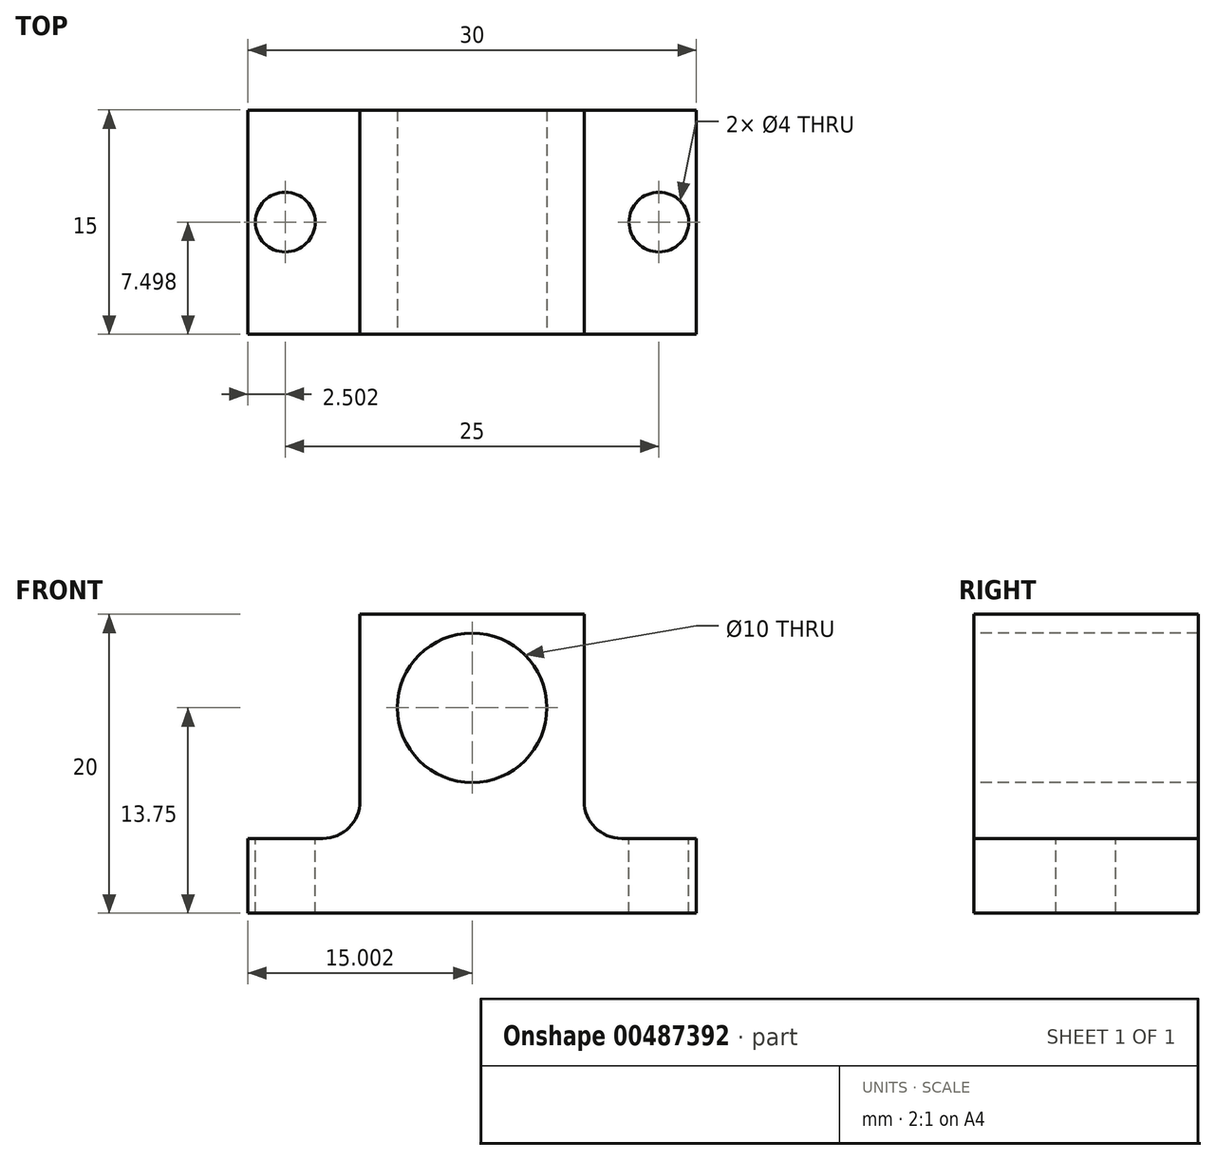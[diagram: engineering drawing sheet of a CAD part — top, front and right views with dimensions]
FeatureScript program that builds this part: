
annotation { "Feature Type Name" : "Feature", "Feature Type Description" : "" }
export const myFeature = defineFeature(function(context is Context, id is Id, definition is map)
    precondition{}
    {
        {
            var Q0;
            Q0=qCreatedBy(makeId("Top.planeOp"),FACE);
            var sketch = newSketch(context, id + "F0", { "sketchPlane" : qUnion([Q0])});
            skLineSegment(sketch, "E0.bottom", {"start": v(-19.82, 4.3) * mm, "end": v(10.18, 4.3) * mm});
            skLineSegment(sketch, "E0.top", {"start": v(-19.82, -10.7) * mm, "end": v(10.18, -10.7) * mm});
            skLineSegment(sketch, "E0.left", {"start": v(-19.82, 4.3) * mm, "end": v(-19.82, -10.7) * mm});
            skLineSegment(sketch, "E0.right", {"start": v(10.18, 4.3) * mm, "end": v(10.18, -10.7) * mm});
            skSolve(sketch);
        }
        {
            var Q0;
            Q0 = qSketchRegion(id + "F0", true);
            extrude(context, id + "F1", {"entities" : qUnion([Q0]), "depth" : 20 * mm});
        }
        {
            var Q0;
            Q0=makeQuery(id+"F1.opExtrude","SWEPT_FACE",FACE,{"disambiguationData":[OSD([sQuery(id+"F0.wireOp",EDGE,"E0.top")])]});
            var sketch = newSketch(context, id + "F2", { "sketchPlane" : qUnion([Q0])});
            skLineSegment(sketch, "E1.bottom", {"start": v(-19.82, 20) * mm, "end": v(-12.32, 20) * mm});
            skLineSegment(sketch, "E1.top", {"start": v(-19.82, 5) * mm, "end": v(-12.32, 5) * mm});
            skLineSegment(sketch, "E1.left", {"start": v(-19.82, 20) * mm, "end": v(-19.82, 5) * mm});
            skLineSegment(sketch, "E1.right", {"start": v(-12.32, 20) * mm, "end": v(-12.32, 5) * mm});
            skLineSegment(sketch, "E2.bottom", {"start": v(10.18, 20) * mm, "end": v(2.68, 20) * mm});
            skLineSegment(sketch, "E2.top", {"start": v(10.18, 5) * mm, "end": v(2.68, 5) * mm});
            skLineSegment(sketch, "E2.left", {"start": v(10.18, 20) * mm, "end": v(10.18, 5) * mm});
            skLineSegment(sketch, "E2.right", {"start": v(2.68, 20) * mm, "end": v(2.68, 5) * mm});
            skSolve(sketch);
        }
        {
            var Q0;
            Q0=makeQuery(id+"F2.imprint","IMPRINT",FACE,{"disambiguationData":[TD([[makeQuery(id+"F2.imprint","IMPRINT",EDGE,{"derivedFrom":sQuery(id+"F2.wireOp",EDGE,"E1.bottom")}),-1.0]])]});
            var Q1;
            Q1=makeQuery(id+"F2.imprint","IMPRINT",FACE,{"disambiguationData":[TD([[makeQuery(id+"F2.imprint","IMPRINT",EDGE,{"derivedFrom":sQuery(id+"F2.wireOp",EDGE,"E2.bottom")}),-1.0]])]});
            extrude(context, id + "F3", {"entities" : qUnion([Q0, Q1]), "operationType" : NewBodyOperationType.REMOVE, "endBound" : BoundingType.THROUGH_ALL, "oppositeDirection" : true, "depth" : 25 * mm});
        }
        {
            var Q0;
            Q0=makeQuery(id+"F3.boolean.opBoolean","COPY",EDGE,{"derivedFrom":makeQuery(id+"F3.opExtrude","SWEPT_EDGE",EDGE,{"disambiguationData":[OSD([sQuery(id+"F2.wireOp",EDGE,"E2.top"),sQuery(id+"F2.wireOp",EDGE,"E2.right")])]})});
            var Q1;
            Q1=makeQuery(id+"F3.boolean.opBoolean","COPY",EDGE,{"derivedFrom":makeQuery(id+"F3.opExtrude","SWEPT_EDGE",EDGE,{"disambiguationData":[OSD([sQuery(id+"F2.wireOp",EDGE,"E1.top"),sQuery(id+"F2.wireOp",EDGE,"E1.right")])]})});
            fillet(context, id + "F4", {"entities" : qUnion([Q0, Q1]), "radius" : 2.5 * mm, "tangentPropagation" : true, "allowEdgeOverflow" : false});
        }
        {
            var Q0;
            Q0=makeQuery(id+"F1.opExtrude","SWEPT_FACE",FACE,{"disambiguationData":[OSD([sQuery(id+"F0.wireOp",EDGE,"E0.top")])]});
            var sketch = newSketch(context, id + "F5", { "sketchPlane" : qUnion([Q0])});
            skLineSegment(sketch, "E3", {"start": v(-14.82, 5) * mm, "end": v(5.18, 5) * mm});
            skCircle(sketch, "E4", {"center": v(-4.82, 13.75) * mm, "radius": 5 * mm});
            skPoint(sketch, "E4.centerSnap0", {"position": v(2.68, 13.75) * mm});
            skPoint(sketch, "E4.centerSnap1", {"position": v(-4.82, 20) * mm});
            skSolve(sketch);
        }
        {
            var Q0;
            Q0=makeQuery(id+"F5.imprint","IMPRINT",FACE,{"disambiguationData":[TD([[makeQuery(id+"F5.imprint","IMPRINT",EDGE,{"derivedFrom":sQuery(id+"F5.wireOp",EDGE,"E4")}),1.0]])]});
            extrude(context, id + "F6", {"entities" : qUnion([Q0]), "operationType" : NewBodyOperationType.REMOVE, "endBound" : BoundingType.THROUGH_ALL, "oppositeDirection" : true, "depth" : 25 * mm});
        }
        {
            var Q0;
            Q0=makeQuery(id+"F3.boolean.opBoolean","COPY",FACE,{"derivedFrom":makeQuery(id+"F3.opExtrude","SWEPT_FACE",FACE,{"disambiguationData":[OSD([sQuery(id+"F2.wireOp",EDGE,"E2.top")])]})});
            var sketch = newSketch(context, id + "F7", { "sketchPlane" : qUnion([Q0])});
            skCircle(sketch, "E5", {"center": v(7.68, -3.2) * mm, "radius": 2 * mm});
            skPoint(sketch, "E5.centerSnap0", {"position": v(7.68, 4.3) * mm});
            skPoint(sketch, "E5.centerSnap1", {"position": v(5.18, -3.2) * mm});
            skSolve(sketch);
        }
        {
            var Q0;
            Q0=makeQuery(id+"F7.imprint","IMPRINT",FACE,{"disambiguationData":[TD([[makeQuery(id+"F7.imprint","IMPRINT",EDGE,{"derivedFrom":sQuery(id+"F7.wireOp",EDGE,"E5")}),1.0]])]});
            extrude(context, id + "F8", {"entities" : qUnion([Q0]), "operationType" : NewBodyOperationType.REMOVE, "endBound" : BoundingType.THROUGH_ALL, "oppositeDirection" : true, "depth" : 25 * mm});
        }
        {
            var Q0;
            Q0=makeQuery(id+"F3.boolean.opBoolean","COPY",FACE,{"derivedFrom":makeQuery(id+"F3.opExtrude","SWEPT_FACE",FACE,{"disambiguationData":[OSD([sQuery(id+"F2.wireOp",EDGE,"E1.top")])]})});
            var sketch = newSketch(context, id + "F9", { "sketchPlane" : qUnion([Q0])});
            skCircle(sketch, "E6", {"center": v(-17.32, -3.2) * mm, "radius": 2 * mm});
            skPoint(sketch, "E6.centerSnap0", {"position": v(-14.82, -3.2) * mm});
            skPoint(sketch, "E6.centerSnap1", {"position": v(-17.32, -10.7) * mm});
            skSolve(sketch);
        }
        {
            var Q0;
            Q0=makeQuery(id+"F9.imprint","IMPRINT",FACE,{"disambiguationData":[TD([[makeQuery(id+"F9.imprint","IMPRINT",EDGE,{"derivedFrom":sQuery(id+"F9.wireOp",EDGE,"E6")}),1.0]])]});
            extrude(context, id + "F10", {"entities" : qUnion([Q0]), "operationType" : NewBodyOperationType.REMOVE, "endBound" : BoundingType.THROUGH_ALL, "oppositeDirection" : true, "depth" : 25 * mm});
        }
    });
